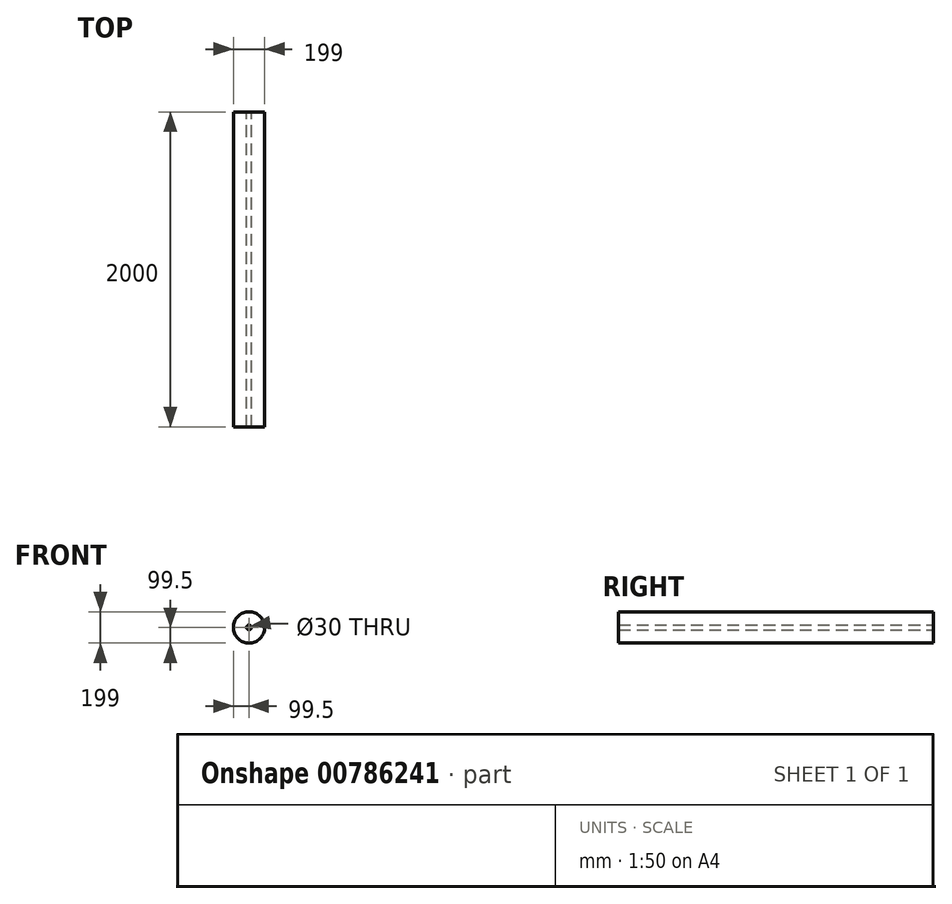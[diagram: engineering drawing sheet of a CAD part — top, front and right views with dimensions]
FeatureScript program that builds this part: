
annotation { "Feature Type Name" : "Feature", "Feature Type Description" : "" }
export const myFeature = defineFeature(function(context is Context, id is Id, definition is map)
    precondition{}
    {
        {
            var Q0;
            Q0=qCreatedBy(makeId("Front.planeOp"),FACE);
            var sketch = newSketch(context, id + "F0", { "sketchPlane" : qUnion([Q0])});
            skCircle(sketch, "E0", {"center": v(0, 0) * mm, "radius": 15 * mm});
            skCircle(sketch, "E1", {"center": v(0, 0) * mm, "radius": 99.5 * mm});
            skCircle(sketch, "E2", {"center": v(0, 0) * mm, "radius": 53.4 * mm});
            skSolve(sketch);
        }
        {
            var Q0;
            Q0=makeQuery(id+"F0.imprint","IMPRINT",FACE,{"disambiguationData":[TD([[makeQuery(id+"F0.imprint","IMPRINT",EDGE,{"derivedFrom":sQuery(id+"F0.wireOp",EDGE,"E0")}),-1.0]])]});
            var Q1;
            Q1=makeQuery(id+"F0.imprint","IMPRINT",FACE,{"disambiguationData":[TD([[makeQuery(id+"F0.imprint","IMPRINT",EDGE,{"derivedFrom":sQuery(id+"F0.wireOp",EDGE,"E1")}),1.0]])]});
            extrude(context, id + "F1", {"entities" : qUnion([Q0, Q1]), "endBound" : BoundingType.SYMMETRIC, "depth" : 2000 * mm, "offsetDistance" : 25 * mm});
        }
    });
